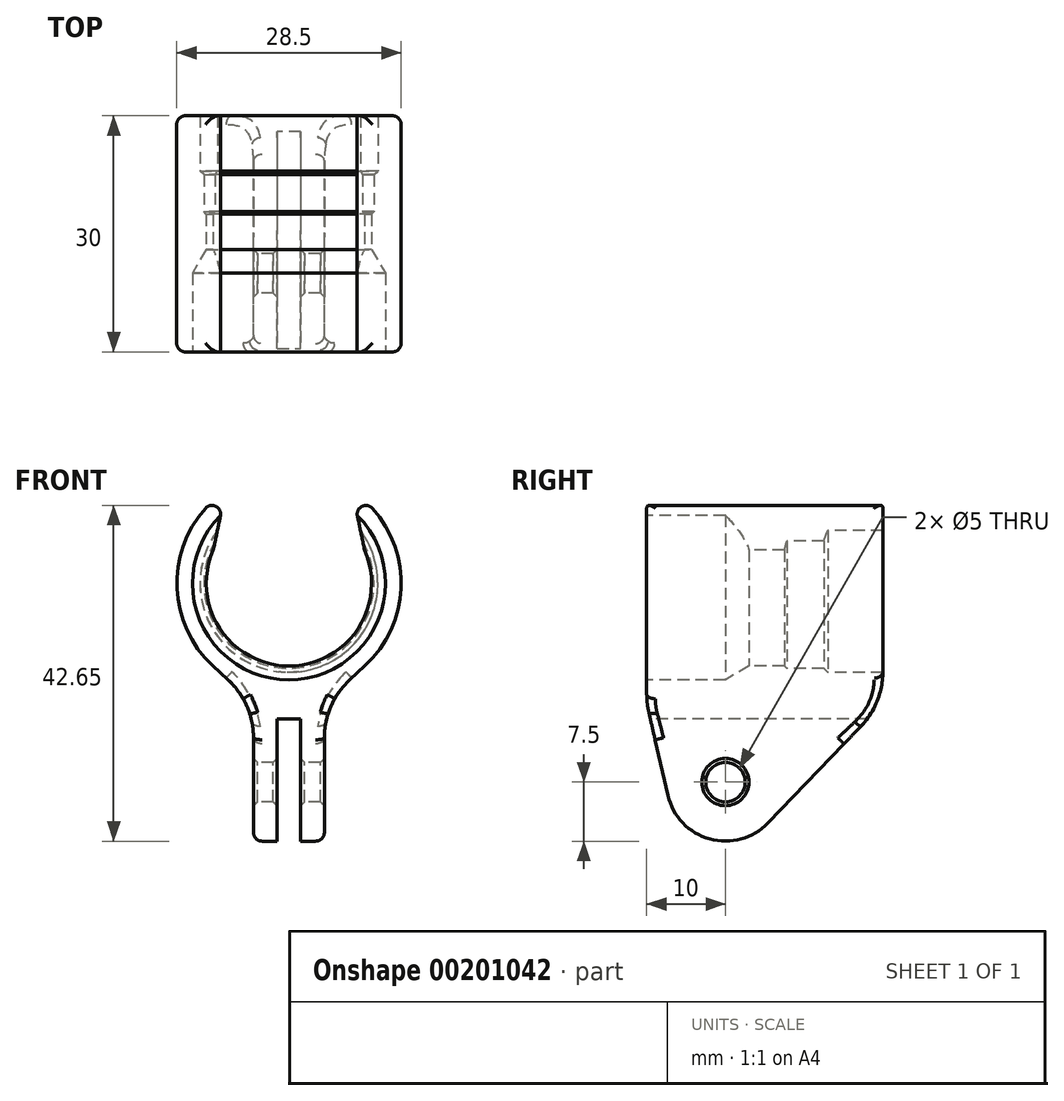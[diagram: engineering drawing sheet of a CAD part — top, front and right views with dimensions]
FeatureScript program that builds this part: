
annotation { "Feature Type Name" : "Feature", "Feature Type Description" : "" }
export const myFeature = defineFeature(function(context is Context, id is Id, definition is map)
    precondition{}
    {
        {
            var Q0;
            Q0=qCreatedBy(makeId("Right.planeOp"),FACE);
            var sketch = newSketch(context, id + "F0", { "sketchPlane" : qUnion([Q0])});
            skLineSegment(sketch, "E0", {"start": v(-10, 12.25) * mm, "end": v(-10, 14.25) * mm});
            skLineSegment(sketch, "E1", {"start": v(-10, 14.25) * mm, "end": v(20, 14.25) * mm});
            skLineSegment(sketch, "E2", {"start": v(20, 14.25) * mm, "end": v(20, 11.3) * mm});
            skLineSegment(sketch, "E3", {"start": v(20, 11.3) * mm, "end": v(13, 11.3) * mm});
            skLineSegment(sketch, "E4", {"start": v(13, 11.3) * mm, "end": v(13, 10.8) * mm});
            skLineSegment(sketch, "E5", {"start": v(13, 10.8) * mm, "end": v(8, 10.8) * mm});
            skLineSegment(sketch, "E6", {"start": v(8, 10.8) * mm, "end": v(8, 10.5) * mm});
            skLineSegment(sketch, "E7", {"start": v(8, 10.5) * mm, "end": v(3, 10.5) * mm});
            skLineSegment(sketch, "E8", {"start": v(0, 12.25) * mm, "end": v(-10, 12.25) * mm});
            skLineSegment(sketch, "E9", {"start": v(3, 10.5) * mm, "end": v(0, 12.25) * mm});
            skLineSegment(sketch, "E10", {"start": v(-10, 0) * mm, "end": v(20, 0) * mm, "construction": true});
            skSolve(sketch);
        }
        {
            var Q0;
            Q0=qSketchRegion(id+"F0",true);
            var Q1;
            Q1=sQuery(id+"F0.wireOp",EDGE,"E10");
            var Q2;
            Q2=sQuery(id+"F0.wireOp",EDGE,"E10");
            revolve(context, id + "F1", {"entities" : qUnion([Q0]), "surfaceEntities" : qUnion([Q1]), "axis" : qUnion([Q2]), "revolveType" : RevolveType.FULL});
        }
        {
            var Q0;
            Q0=qCreatedBy(makeId("Front.planeOp"),FACE);
            var sketch = newSketch(context, id + "F2", { "sketchPlane" : qUnion([Q0])});
            skLineSegment(sketch, "E11.bottom", {"start": v(7.5, 14.25) * mm, "end": v(-7.5, 14.25) * mm});
            skLineSegment(sketch, "E11.top", {"start": v(10.5, 0) * mm, "end": v(-10.5, 0) * mm});
            skLineSegment(sketch, "E11.left", {"start": v(7.5, 14.25) * mm, "end": v(10.5, 0) * mm});
            skLineSegment(sketch, "E11.right", {"start": v(-7.5, 14.25) * mm, "end": v(-10.5, 0) * mm});
            skSolve(sketch);
        }
        {
            var Q0;
            Q0=qSketchRegion(id+"F2",true);
            extrude(context, id + "F3", {"entities" : qUnion([Q0]), "operationType" : NewBodyOperationType.REMOVE, "endBound" : BoundingType.THROUGH_ALL, "oppositeDirection" : true, "depth" : 25 * mm, "hasSecondDirection" : true, "secondDirectionBound" : SecondDirectionBoundingType.THROUGH_ALL, "secondDirectionOppositeDirection" : false, "secondDirectionDepth" : 25 * mm});
        }
        {
            var Q0;
            Q0=qCreatedBy(makeId("Front.planeOp"),FACE);
            var sketch = newSketch(context, id + "F4", { "sketchPlane" : qUnion([Q0])});
            skLineSegment(sketch, "E12", {"start": v(-9.68, -10.46) * mm, "end": v(-4.5, -15.25) * mm});
            skLineSegment(sketch, "E13", {"start": v(-4.5, -15.25) * mm, "end": v(4.5, -15.25) * mm});
            skLineSegment(sketch, "E14", {"start": v(4.5, -15.25) * mm, "end": v(9.68, -10.46) * mm});
            skLineSegment(sketch, "E15", {"start": v(0, -15.25) * mm, "end": v(0, 0) * mm, "construction": true});
            skArc(sketch, "E16.0", {"start": v(-9.68, -10.46) * mm, "mid": v(0, -14.25) * mm, "end": v(9.68, -10.46) * mm});
            skPoint(sketch, "E17.orphan", {"position": v(-8.02, 11.78) * mm});
            skPoint(sketch, "E18.orphan", {"position": v(8.02, 11.78) * mm});
            skSolve(sketch);
        }
        {
            var Q0;
            Q0=makeQuery(id+"F4.imprint","IMPRINT",FACE,{"disambiguationData":[TD([[makeQuery(id+"F4.imprint","IMPRINT",EDGE,{"derivedFrom":sQuery(id+"F4.wireOp",EDGE,"E12")}),1.0]])]});
            var Q1;
            Q1=makeQuery(id+"F1.opRevolve","SWEPT_FACE",FACE,{"disambiguationData":[OSD([sQuery(id+"F0.wireOp",EDGE,"E0")])]});
            var Q2;
            Q2=makeQuery(id+"F1.opRevolve","SWEPT_FACE",FACE,{"disambiguationData":[OSD([sQuery(id+"F0.wireOp",EDGE,"E2")])]});
            extrude(context, id + "F5", {"entities" : qUnion([Q0]), "operationType" : NewBodyOperationType.ADD, "endBound" : BoundingType.UP_TO_SURFACE, "endBoundEntityFace" : qUnion([Q1]), "depth" : 2 * mm, "hasSecondDirection" : true, "secondDirectionBound" : SecondDirectionBoundingType.UP_TO_SURFACE, "secondDirectionOppositeDirection" : true, "secondDirectionBoundEntityFace" : qUnion([Q2]), "secondDirectionDepth" : 25 * mm});
        }
        {
            var Q0;
            Q0=qCreatedBy(makeId("Right.planeOp"),FACE);
            var sketch = newSketch(context, id + "F6", { "sketchPlane" : qUnion([Q0])});
            skArc(sketch, "E19", {"start": v(-7.3, -26.93) * mm, "mid": v(-2, -32.48) * mm, "end": v(5.4, -30.44) * mm});
            skCircle(sketch, "E20", {"center": v(0, -25.25) * mm, "radius": 2.5 * mm});
            skLineSegment(sketch, "E21", {"start": v(20, -15.25) * mm, "end": v(5.4, -30.44) * mm});
            skLineSegment(sketch, "E22", {"start": v(-10, -15.25) * mm, "end": v(-7.3, -26.93) * mm});
            skLineSegment(sketch, "E23.0", {"start": v(-10, -15.25) * mm, "end": v(20, -15.25) * mm});
            skSolve(sketch);
        }
        {
            var Q0;
            Q0=qSketchRegion(id+"F6",true);
            var Q1;
            Q1=makeQuery(id+"F5.opExtrude","SWEPT_FACE",FACE,{"disambiguationData":[OSD([sQuery(id+"F4.wireOp",EDGE,"E12")])]});
            extrude(context, id + "F7", {"entities" : qUnion([Q0]), "operationType" : NewBodyOperationType.ADD, "endBoundEntityFace" : qUnion([Q1]), "depth" : 4.5 * mm, "hasSecondDirection" : true, "secondDirectionOppositeDirection" : true, "secondDirectionDepth" : 4.5 * mm});
        }
        {
            var Q0;
            Q0=qCreatedBy(makeId("Front.planeOp"),FACE);
            var sketch = newSketch(context, id + "F8", { "sketchPlane" : qUnion([Q0])});
            skLineSegment(sketch, "E24.top", {"start": v(1.5, -17.25) * mm, "end": v(-1.5, -17.25) * mm});
            skLineSegment(sketch, "E24.left", {"start": v(1.5, -32.75) * mm, "end": v(1.5, -17.25) * mm});
            skLineSegment(sketch, "E24.right", {"start": v(-1.5, -32.75) * mm, "end": v(-1.5, -17.25) * mm});
            skLineSegment(sketch, "E25", {"start": v(0, 0) * mm, "end": v(0, -32.75) * mm, "construction": true});
            skLineSegment(sketch, "E26", {"start": v(1.5, -32.75) * mm, "end": v(-1.5, -32.75) * mm});
            skSolve(sketch);
        }
        {
            var Q0;
            Q0=qSketchRegion(id+"F8",true);
            extrude(context, id + "F9", {"entities" : qUnion([Q0]), "operationType" : NewBodyOperationType.REMOVE, "endBound" : BoundingType.THROUGH_ALL, "oppositeDirection" : true, "depth" : 25 * mm, "hasSecondDirection" : true, "secondDirectionBound" : SecondDirectionBoundingType.THROUGH_ALL, "secondDirectionOppositeDirection" : false, "secondDirectionDepth" : 25 * mm});
        }
        {
            var Q0;
            Q0=makeQuery(id+"F7.boolean.opBoolean","MERGE",EDGE,{"derivedFrom":[makeQuery(id+"F5.opExtrude","TWEAK_EDGE",EDGE,{"derivedFrom":[makeQuery(id+"F4.imprint","IMPRINT",EDGE,{"derivedFrom":sQuery(id+"F4.wireOp",EDGE,"E13")}),makeQuery(id+"F4.imprint","IMPRINT",EDGE,{"derivedFrom":sQuery(id+"F4.wireOp",EDGE,"E14")})]}),makeQuery(id+"F7.opExtrude","CAP_EDGE",EDGE,{"disambiguationData":[OSD([sQuery(id+"F6.wireOp",EDGE,"E23.0")])],"isStart":false})]});
            var Q1;
            Q1=makeQuery(id+"F5.opExtrude","TWEAK_EDGE",EDGE,{"derivedFrom":[makeQuery(id+"F4.imprint","IMPRINT",EDGE,{"derivedFrom":sQuery(id+"F4.wireOp",EDGE,"E14")}),makeQuery(id+"F4.imprint","IMPRINT",EDGE,{"derivedFrom":sQuery(id+"F4.wireOp",EDGE,"E16.0")})]});
            var Q2;
            Q2=makeQuery(id+"F7.boolean.opBoolean","MERGE",EDGE,{"derivedFrom":[makeQuery(id+"F5.opExtrude","TWEAK_EDGE",EDGE,{"derivedFrom":[makeQuery(id+"F4.imprint","IMPRINT",EDGE,{"derivedFrom":sQuery(id+"F4.wireOp",EDGE,"E12")}),makeQuery(id+"F4.imprint","IMPRINT",EDGE,{"derivedFrom":sQuery(id+"F4.wireOp",EDGE,"E13")})]}),makeQuery(id+"F7.opExtrude","CAP_EDGE",EDGE,{"disambiguationData":[OSD([sQuery(id+"F6.wireOp",EDGE,"E23.0")])],"isStart":true})]});
            var Q3;
            Q3=makeQuery(id+"F5.opExtrude","TWEAK_EDGE",EDGE,{"derivedFrom":[makeQuery(id+"F4.imprint","IMPRINT",EDGE,{"derivedFrom":sQuery(id+"F4.wireOp",EDGE,"E12")}),makeQuery(id+"F4.imprint","IMPRINT",EDGE,{"derivedFrom":sQuery(id+"F4.wireOp",EDGE,"E16.0")})]});
            var Q4;
            Q4=makeQuery(id+"F7.boolean.opBoolean","MERGE",EDGE,{"derivedFrom":[makeQuery(id+"F5.opExtrude","CAP_EDGE",EDGE,{"disambiguationData":[OSD([sQuery(id+"F4.wireOp",EDGE,"E13")])],"isStart":true}),makeQuery(id+"F7.opExtrude","SWEPT_EDGE",EDGE,{"disambiguationData":[OSD([sQuery(id+"F6.wireOp",EDGE,"E21"),sQuery(id+"F6.wireOp",EDGE,"E23.0")])]})]});
            var Q5;
            Q5=makeQuery(id+"F7.boolean.opBoolean","MERGE",EDGE,{"derivedFrom":[makeQuery(id+"F5.opExtrude","CAP_EDGE",EDGE,{"disambiguationData":[OSD([sQuery(id+"F4.wireOp",EDGE,"E13")])],"isStart":false}),makeQuery(id+"F7.opExtrude","SWEPT_EDGE",EDGE,{"disambiguationData":[OSD([sQuery(id+"F6.wireOp",EDGE,"E22"),sQuery(id+"F6.wireOp",EDGE,"E23.0")])]})]});
            fillet(context, id + "F10", {"entities" : qUnion([Q0, Q1, Q2, Q3, Q4, Q5]), "radius" : 10 * mm, "tangentPropagation" : true, "allowEdgeOverflow" : false});
        }
        {
            var Q0;
            {var subQ0=sQuery(id+"F0.wireOp",EDGE,"E0");var subQ1=sQuery(id+"F0.wireOp",EDGE,"E1");Q0=makeQuery(id+"F5.boolean.opBoolean","SPLIT",EDGE,{"disambiguationData":[TD([makeQuery(id+"F3.boolean.opBoolean","COPY",FACE,{"derivedFrom":makeQuery(id+"F3.opExtrude","SWEPT_FACE",FACE,{"disambiguationData":[OSD([sQuery(id+"F2.wireOp",EDGE,"E11.right")])]})})])],"derivedFrom":makeQuery(id+"F1.opRevolve","SWEPT_EDGE",EDGE,{"disambiguationData":[OSD([subQ0,subQ1])]})});}
            var Q1;
            Q1=makeQuery(id+"F5.opExtrude","CAP_EDGE",EDGE,{"disambiguationData":[OSD([sQuery(id+"F4.wireOp",EDGE,"E12")])],"isStart":false});
            var Q2;
            {var subQ0=sQuery(id+"F4.wireOp",EDGE,"E12");var subQ1=sQuery(id+"F4.wireOp",EDGE,"E13");Q2=makeQuery(id+"F10.opFillet","BLEND_EDGE",EDGE,{"blendedFrom":[makeQuery(id+"F7.boolean.opBoolean","MERGE",EDGE,{"derivedFrom":[makeQuery(id+"F5.opExtrude","TWEAK_EDGE",EDGE,{"derivedFrom":[makeQuery(id+"F4.imprint","IMPRINT",EDGE,{"derivedFrom":subQ0}),makeQuery(id+"F4.imprint","IMPRINT",EDGE,{"derivedFrom":subQ1})]}),makeQuery(id+"F7.opExtrude","CAP_EDGE",EDGE,{"disambiguationData":[OSD([sQuery(id+"F6.wireOp",EDGE,"E23.0")])],"isStart":true})]}),makeQuery(id+"F5.boolean.opBoolean","MERGE",FACE,{"derivedFrom":[makeQuery(id+"F1.opRevolve","SWEPT_FACE",FACE,{"disambiguationData":[OSD([sQuery(id+"F0.wireOp",EDGE,"E0")])]}),makeQuery(id+"F5.opExtrude","CAP_FACE",FACE,{"disambiguationData":[OSD([subQ0,subQ1,sQuery(id+"F4.wireOp",EDGE,"E14"),sQuery(id+"F4.wireOp",EDGE,"E16.0")])],"isStart":false})]})],"blendedInto":[makeQuery(id+"F5.boolean.opBoolean","MERGE",FACE,{"derivedFrom":[makeQuery(id+"F1.opRevolve","SWEPT_FACE",FACE,{"disambiguationData":[OSD([sQuery(id+"F0.wireOp",EDGE,"E0")])]}),makeQuery(id+"F5.opExtrude","CAP_FACE",FACE,{"disambiguationData":[OSD([subQ0,subQ1,sQuery(id+"F4.wireOp",EDGE,"E14"),sQuery(id+"F4.wireOp",EDGE,"E16.0")])],"isStart":false})]})]});}
            var Q3;
            Q3=makeQuery(id+"F10.opFillet","BLEND_EDGE",EDGE,{"blendedFrom":[makeQuery(id+"F7.boolean.opBoolean","MERGE",EDGE,{"derivedFrom":[makeQuery(id+"F5.opExtrude","TWEAK_EDGE",EDGE,{"derivedFrom":[makeQuery(id+"F4.imprint","IMPRINT",EDGE,{"derivedFrom":sQuery(id+"F4.wireOp",EDGE,"E12")}),makeQuery(id+"F4.imprint","IMPRINT",EDGE,{"derivedFrom":sQuery(id+"F4.wireOp",EDGE,"E13")})]}),makeQuery(id+"F7.opExtrude","CAP_EDGE",EDGE,{"disambiguationData":[OSD([sQuery(id+"F6.wireOp",EDGE,"E23.0")])],"isStart":true})]}),makeQuery(id+"F7.opExtrude","SWEPT_FACE",FACE,{"disambiguationData":[OSD([sQuery(id+"F6.wireOp",EDGE,"E22")])]})],"blendedInto":[makeQuery(id+"F7.opExtrude","SWEPT_FACE",FACE,{"disambiguationData":[OSD([sQuery(id+"F6.wireOp",EDGE,"E22")])]})]});
            var Q4;
            Q4=makeQuery(id+"F7.opExtrude","CAP_EDGE",EDGE,{"disambiguationData":[OSD([sQuery(id+"F6.wireOp",EDGE,"E22")])],"isStart":true});
            var Q5;
            Q5=makeQuery(id+"F7.opExtrude","CAP_EDGE",EDGE,{"disambiguationData":[OSD([sQuery(id+"F6.wireOp",EDGE,"E19")])],"isStart":true});
            var Q6;
            Q6=makeQuery(id+"F7.opExtrude","CAP_EDGE",EDGE,{"disambiguationData":[OSD([sQuery(id+"F6.wireOp",EDGE,"E21")])],"isStart":true});
            var Q7;
            Q7=makeQuery(id+"F10.opFillet","BLEND_EDGE",EDGE,{"blendedFrom":[makeQuery(id+"F7.boolean.opBoolean","MERGE",EDGE,{"derivedFrom":[makeQuery(id+"F5.opExtrude","TWEAK_EDGE",EDGE,{"derivedFrom":[makeQuery(id+"F4.imprint","IMPRINT",EDGE,{"derivedFrom":sQuery(id+"F4.wireOp",EDGE,"E12")}),makeQuery(id+"F4.imprint","IMPRINT",EDGE,{"derivedFrom":sQuery(id+"F4.wireOp",EDGE,"E13")})]}),makeQuery(id+"F7.opExtrude","CAP_EDGE",EDGE,{"disambiguationData":[OSD([sQuery(id+"F6.wireOp",EDGE,"E23.0")])],"isStart":true})]}),makeQuery(id+"F7.opExtrude","SWEPT_FACE",FACE,{"disambiguationData":[OSD([sQuery(id+"F6.wireOp",EDGE,"E21")])]})],"blendedInto":[makeQuery(id+"F7.opExtrude","SWEPT_FACE",FACE,{"disambiguationData":[OSD([sQuery(id+"F6.wireOp",EDGE,"E21")])]})]});
            var Q8;
            {var subQ0=sQuery(id+"F4.wireOp",EDGE,"E12");var subQ1=sQuery(id+"F4.wireOp",EDGE,"E13");Q8=makeQuery(id+"F10.opFillet","BLEND_EDGE",EDGE,{"blendedFrom":[makeQuery(id+"F7.boolean.opBoolean","MERGE",EDGE,{"derivedFrom":[makeQuery(id+"F5.opExtrude","TWEAK_EDGE",EDGE,{"derivedFrom":[makeQuery(id+"F4.imprint","IMPRINT",EDGE,{"derivedFrom":subQ0}),makeQuery(id+"F4.imprint","IMPRINT",EDGE,{"derivedFrom":subQ1})]}),makeQuery(id+"F7.opExtrude","CAP_EDGE",EDGE,{"disambiguationData":[OSD([sQuery(id+"F6.wireOp",EDGE,"E23.0")])],"isStart":true})]}),makeQuery(id+"F5.boolean.opBoolean","MERGE",FACE,{"derivedFrom":[makeQuery(id+"F1.opRevolve","SWEPT_FACE",FACE,{"disambiguationData":[OSD([sQuery(id+"F0.wireOp",EDGE,"E2")])]}),makeQuery(id+"F5.opExtrude","CAP_FACE",FACE,{"disambiguationData":[OSD([subQ0,subQ1,sQuery(id+"F4.wireOp",EDGE,"E14"),sQuery(id+"F4.wireOp",EDGE,"E16.0")])],"isStart":true})]})],"blendedInto":[makeQuery(id+"F5.boolean.opBoolean","MERGE",FACE,{"derivedFrom":[makeQuery(id+"F1.opRevolve","SWEPT_FACE",FACE,{"disambiguationData":[OSD([sQuery(id+"F0.wireOp",EDGE,"E2")])]}),makeQuery(id+"F5.opExtrude","CAP_FACE",FACE,{"disambiguationData":[OSD([subQ0,subQ1,sQuery(id+"F4.wireOp",EDGE,"E14"),sQuery(id+"F4.wireOp",EDGE,"E16.0")])],"isStart":true})]})]});}
            var Q9;
            Q9=makeQuery(id+"F5.opExtrude","CAP_EDGE",EDGE,{"disambiguationData":[OSD([sQuery(id+"F4.wireOp",EDGE,"E12")])],"isStart":true});
            var Q10;
            {var subQ0=sQuery(id+"F0.wireOp",EDGE,"E1");var subQ1=sQuery(id+"F0.wireOp",EDGE,"E2");Q10=makeQuery(id+"F5.boolean.opBoolean","SPLIT",EDGE,{"disambiguationData":[TD([makeQuery(id+"F3.boolean.opBoolean","COPY",FACE,{"derivedFrom":makeQuery(id+"F3.opExtrude","SWEPT_FACE",FACE,{"disambiguationData":[OSD([sQuery(id+"F2.wireOp",EDGE,"E11.right")])]})})])],"derivedFrom":makeQuery(id+"F1.opRevolve","SWEPT_EDGE",EDGE,{"disambiguationData":[OSD([subQ0,subQ1])]})});}
            var Q11;
            Q11=makeQuery(id+"F3.boolean.opBoolean","INTERSECT",EDGE,{"derivedFrom":[makeQuery(id+"F1.opRevolve","SWEPT_FACE",FACE,{"disambiguationData":[OSD([sQuery(id+"F0.wireOp",EDGE,"E1")])]}),makeQuery(id+"F3.opExtrude","SWEPT_FACE",FACE,{"disambiguationData":[OSD([sQuery(id+"F2.wireOp",EDGE,"E11.right")])]})]});
            var Q12;
            Q12=makeQuery(id+"F3.boolean.opBoolean","INTERSECT",EDGE,{"derivedFrom":[makeQuery(id+"F1.opRevolve","SWEPT_FACE",FACE,{"disambiguationData":[OSD([sQuery(id+"F0.wireOp",EDGE,"E1")])]}),makeQuery(id+"F3.opExtrude","SWEPT_FACE",FACE,{"disambiguationData":[OSD([sQuery(id+"F2.wireOp",EDGE,"E11.left")])]})]});
            var Q13;
            {var subQ0=sQuery(id+"F0.wireOp",EDGE,"E0");var subQ1=sQuery(id+"F0.wireOp",EDGE,"E1");Q13=makeQuery(id+"F5.boolean.opBoolean","SPLIT",EDGE,{"disambiguationData":[TD([makeQuery(id+"F3.boolean.opBoolean","COPY",FACE,{"derivedFrom":makeQuery(id+"F3.opExtrude","SWEPT_FACE",FACE,{"disambiguationData":[OSD([sQuery(id+"F2.wireOp",EDGE,"E11.left")])]})})])],"derivedFrom":makeQuery(id+"F1.opRevolve","SWEPT_EDGE",EDGE,{"disambiguationData":[OSD([subQ0,subQ1])]})});}
            var Q14;
            Q14=makeQuery(id+"F5.opExtrude","CAP_EDGE",EDGE,{"disambiguationData":[OSD([sQuery(id+"F4.wireOp",EDGE,"E14")])],"isStart":false});
            var Q15;
            {var subQ0=sQuery(id+"F4.wireOp",EDGE,"E13");var subQ1=sQuery(id+"F4.wireOp",EDGE,"E14");Q15=makeQuery(id+"F10.opFillet","BLEND_EDGE",EDGE,{"blendedFrom":[makeQuery(id+"F7.boolean.opBoolean","MERGE",EDGE,{"derivedFrom":[makeQuery(id+"F5.opExtrude","TWEAK_EDGE",EDGE,{"derivedFrom":[makeQuery(id+"F4.imprint","IMPRINT",EDGE,{"derivedFrom":subQ0}),makeQuery(id+"F4.imprint","IMPRINT",EDGE,{"derivedFrom":subQ1})]}),makeQuery(id+"F7.opExtrude","CAP_EDGE",EDGE,{"disambiguationData":[OSD([sQuery(id+"F6.wireOp",EDGE,"E23.0")])],"isStart":false})]}),makeQuery(id+"F5.boolean.opBoolean","MERGE",FACE,{"derivedFrom":[makeQuery(id+"F1.opRevolve","SWEPT_FACE",FACE,{"disambiguationData":[OSD([sQuery(id+"F0.wireOp",EDGE,"E0")])]}),makeQuery(id+"F5.opExtrude","CAP_FACE",FACE,{"disambiguationData":[OSD([sQuery(id+"F4.wireOp",EDGE,"E12"),subQ0,subQ1,sQuery(id+"F4.wireOp",EDGE,"E16.0")])],"isStart":false})]})],"blendedInto":[makeQuery(id+"F5.boolean.opBoolean","MERGE",FACE,{"derivedFrom":[makeQuery(id+"F1.opRevolve","SWEPT_FACE",FACE,{"disambiguationData":[OSD([sQuery(id+"F0.wireOp",EDGE,"E0")])]}),makeQuery(id+"F5.opExtrude","CAP_FACE",FACE,{"disambiguationData":[OSD([sQuery(id+"F4.wireOp",EDGE,"E12"),subQ0,subQ1,sQuery(id+"F4.wireOp",EDGE,"E16.0")])],"isStart":false})]})]});}
            var Q16;
            Q16=makeQuery(id+"F10.opFillet","BLEND_EDGE",EDGE,{"blendedFrom":[makeQuery(id+"F7.boolean.opBoolean","MERGE",EDGE,{"derivedFrom":[makeQuery(id+"F5.opExtrude","TWEAK_EDGE",EDGE,{"derivedFrom":[makeQuery(id+"F4.imprint","IMPRINT",EDGE,{"derivedFrom":sQuery(id+"F4.wireOp",EDGE,"E13")}),makeQuery(id+"F4.imprint","IMPRINT",EDGE,{"derivedFrom":sQuery(id+"F4.wireOp",EDGE,"E14")})]}),makeQuery(id+"F7.opExtrude","CAP_EDGE",EDGE,{"disambiguationData":[OSD([sQuery(id+"F6.wireOp",EDGE,"E23.0")])],"isStart":false})]}),makeQuery(id+"F7.opExtrude","SWEPT_FACE",FACE,{"disambiguationData":[OSD([sQuery(id+"F6.wireOp",EDGE,"E22")])]})],"blendedInto":[makeQuery(id+"F7.opExtrude","SWEPT_FACE",FACE,{"disambiguationData":[OSD([sQuery(id+"F6.wireOp",EDGE,"E22")])]})]});
            var Q17;
            Q17=makeQuery(id+"F7.opExtrude","CAP_EDGE",EDGE,{"disambiguationData":[OSD([sQuery(id+"F6.wireOp",EDGE,"E22")])],"isStart":false});
            var Q18;
            Q18=makeQuery(id+"F7.opExtrude","CAP_EDGE",EDGE,{"disambiguationData":[OSD([sQuery(id+"F6.wireOp",EDGE,"E19")])],"isStart":false});
            var Q19;
            Q19=makeQuery(id+"F7.opExtrude","CAP_EDGE",EDGE,{"disambiguationData":[OSD([sQuery(id+"F6.wireOp",EDGE,"E21")])],"isStart":false});
            var Q20;
            Q20=makeQuery(id+"F10.opFillet","BLEND_EDGE",EDGE,{"blendedFrom":[makeQuery(id+"F7.boolean.opBoolean","MERGE",EDGE,{"derivedFrom":[makeQuery(id+"F5.opExtrude","TWEAK_EDGE",EDGE,{"derivedFrom":[makeQuery(id+"F4.imprint","IMPRINT",EDGE,{"derivedFrom":sQuery(id+"F4.wireOp",EDGE,"E13")}),makeQuery(id+"F4.imprint","IMPRINT",EDGE,{"derivedFrom":sQuery(id+"F4.wireOp",EDGE,"E14")})]}),makeQuery(id+"F7.opExtrude","CAP_EDGE",EDGE,{"disambiguationData":[OSD([sQuery(id+"F6.wireOp",EDGE,"E23.0")])],"isStart":false})]}),makeQuery(id+"F7.opExtrude","SWEPT_FACE",FACE,{"disambiguationData":[OSD([sQuery(id+"F6.wireOp",EDGE,"E21")])]})],"blendedInto":[makeQuery(id+"F7.opExtrude","SWEPT_FACE",FACE,{"disambiguationData":[OSD([sQuery(id+"F6.wireOp",EDGE,"E21")])]})]});
            var Q21;
            {var subQ0=sQuery(id+"F4.wireOp",EDGE,"E13");var subQ1=sQuery(id+"F4.wireOp",EDGE,"E14");Q21=makeQuery(id+"F10.opFillet","BLEND_EDGE",EDGE,{"blendedFrom":[makeQuery(id+"F7.boolean.opBoolean","MERGE",EDGE,{"derivedFrom":[makeQuery(id+"F5.opExtrude","TWEAK_EDGE",EDGE,{"derivedFrom":[makeQuery(id+"F4.imprint","IMPRINT",EDGE,{"derivedFrom":subQ0}),makeQuery(id+"F4.imprint","IMPRINT",EDGE,{"derivedFrom":subQ1})]}),makeQuery(id+"F7.opExtrude","CAP_EDGE",EDGE,{"disambiguationData":[OSD([sQuery(id+"F6.wireOp",EDGE,"E23.0")])],"isStart":false})]}),makeQuery(id+"F5.boolean.opBoolean","MERGE",FACE,{"derivedFrom":[makeQuery(id+"F1.opRevolve","SWEPT_FACE",FACE,{"disambiguationData":[OSD([sQuery(id+"F0.wireOp",EDGE,"E2")])]}),makeQuery(id+"F5.opExtrude","CAP_FACE",FACE,{"disambiguationData":[OSD([sQuery(id+"F4.wireOp",EDGE,"E12"),subQ0,subQ1,sQuery(id+"F4.wireOp",EDGE,"E16.0")])],"isStart":true})]})],"blendedInto":[makeQuery(id+"F5.boolean.opBoolean","MERGE",FACE,{"derivedFrom":[makeQuery(id+"F1.opRevolve","SWEPT_FACE",FACE,{"disambiguationData":[OSD([sQuery(id+"F0.wireOp",EDGE,"E2")])]}),makeQuery(id+"F5.opExtrude","CAP_FACE",FACE,{"disambiguationData":[OSD([sQuery(id+"F4.wireOp",EDGE,"E12"),subQ0,subQ1,sQuery(id+"F4.wireOp",EDGE,"E16.0")])],"isStart":true})]})]});}
            var Q22;
            Q22=makeQuery(id+"F5.opExtrude","CAP_EDGE",EDGE,{"disambiguationData":[OSD([sQuery(id+"F4.wireOp",EDGE,"E14")])],"isStart":true});
            var Q23;
            {var subQ0=sQuery(id+"F0.wireOp",EDGE,"E1");var subQ1=sQuery(id+"F0.wireOp",EDGE,"E2");Q23=makeQuery(id+"F5.boolean.opBoolean","SPLIT",EDGE,{"disambiguationData":[TD([makeQuery(id+"F3.boolean.opBoolean","COPY",FACE,{"derivedFrom":makeQuery(id+"F3.opExtrude","SWEPT_FACE",FACE,{"disambiguationData":[OSD([sQuery(id+"F2.wireOp",EDGE,"E11.left")])]})})])],"derivedFrom":makeQuery(id+"F1.opRevolve","SWEPT_EDGE",EDGE,{"disambiguationData":[OSD([subQ0,subQ1])]})});}
            fillet(context, id + "F11", {"entities" : qUnion([Q0, Q1, Q2, Q3, Q4, Q5, Q6, Q7, Q8, Q9, Q10, Q11, Q12, Q13, Q14, Q15, Q16, Q17, Q18, Q19, Q20, Q21, Q22, Q23]), "radius" : 1.1 * mm, "tangentPropagation" : true, "allowEdgeOverflow" : false});
        }
        {
            var Q0;
            Q0=makeQuery(id+"F1.opRevolve","SWEPT_EDGE",EDGE,{"disambiguationData":[OSD([sQuery(id+"F0.wireOp",EDGE,"E4"),sQuery(id+"F0.wireOp",EDGE,"E5")])]});
            var Q1;
            Q1=makeQuery(id+"F1.opRevolve","SWEPT_EDGE",EDGE,{"disambiguationData":[OSD([sQuery(id+"F0.wireOp",EDGE,"E6"),sQuery(id+"F0.wireOp",EDGE,"E7")])]});
            var Q2;
            Q2=makeQuery(id+"F7.opExtrude","CAP_EDGE",EDGE,{"disambiguationData":[OSD([sQuery(id+"F6.wireOp",EDGE,"E20")])],"isStart":false});
            var Q3;
            Q3=makeQuery(id+"F9.boolean.opBoolean","INTERSECT",EDGE,{"derivedFrom":[makeQuery(id+"F7.opExtrude","SWEPT_FACE",FACE,{"disambiguationData":[OSD([sQuery(id+"F6.wireOp",EDGE,"E20")])]}),makeQuery(id+"F9.opExtrude","SWEPT_FACE",FACE,{"disambiguationData":[OSD([sQuery(id+"F8.wireOp",EDGE,"E24.left")])]})]});
            var Q4;
            Q4=makeQuery(id+"F9.boolean.opBoolean","INTERSECT",EDGE,{"derivedFrom":[makeQuery(id+"F7.opExtrude","SWEPT_FACE",FACE,{"disambiguationData":[OSD([sQuery(id+"F6.wireOp",EDGE,"E20")])]}),makeQuery(id+"F9.opExtrude","SWEPT_FACE",FACE,{"disambiguationData":[OSD([sQuery(id+"F8.wireOp",EDGE,"E24.right")])]})]});
            var Q5;
            Q5=makeQuery(id+"F7.opExtrude","CAP_EDGE",EDGE,{"disambiguationData":[OSD([sQuery(id+"F6.wireOp",EDGE,"E20")])],"isStart":true});
            chamfer(context, id + "F12", {"entities" : qUnion([Q0, Q1, Q2, Q3, Q4, Q5]), "width" : 0.5 * mm, "tangentPropagation" : true});
        }
    });
